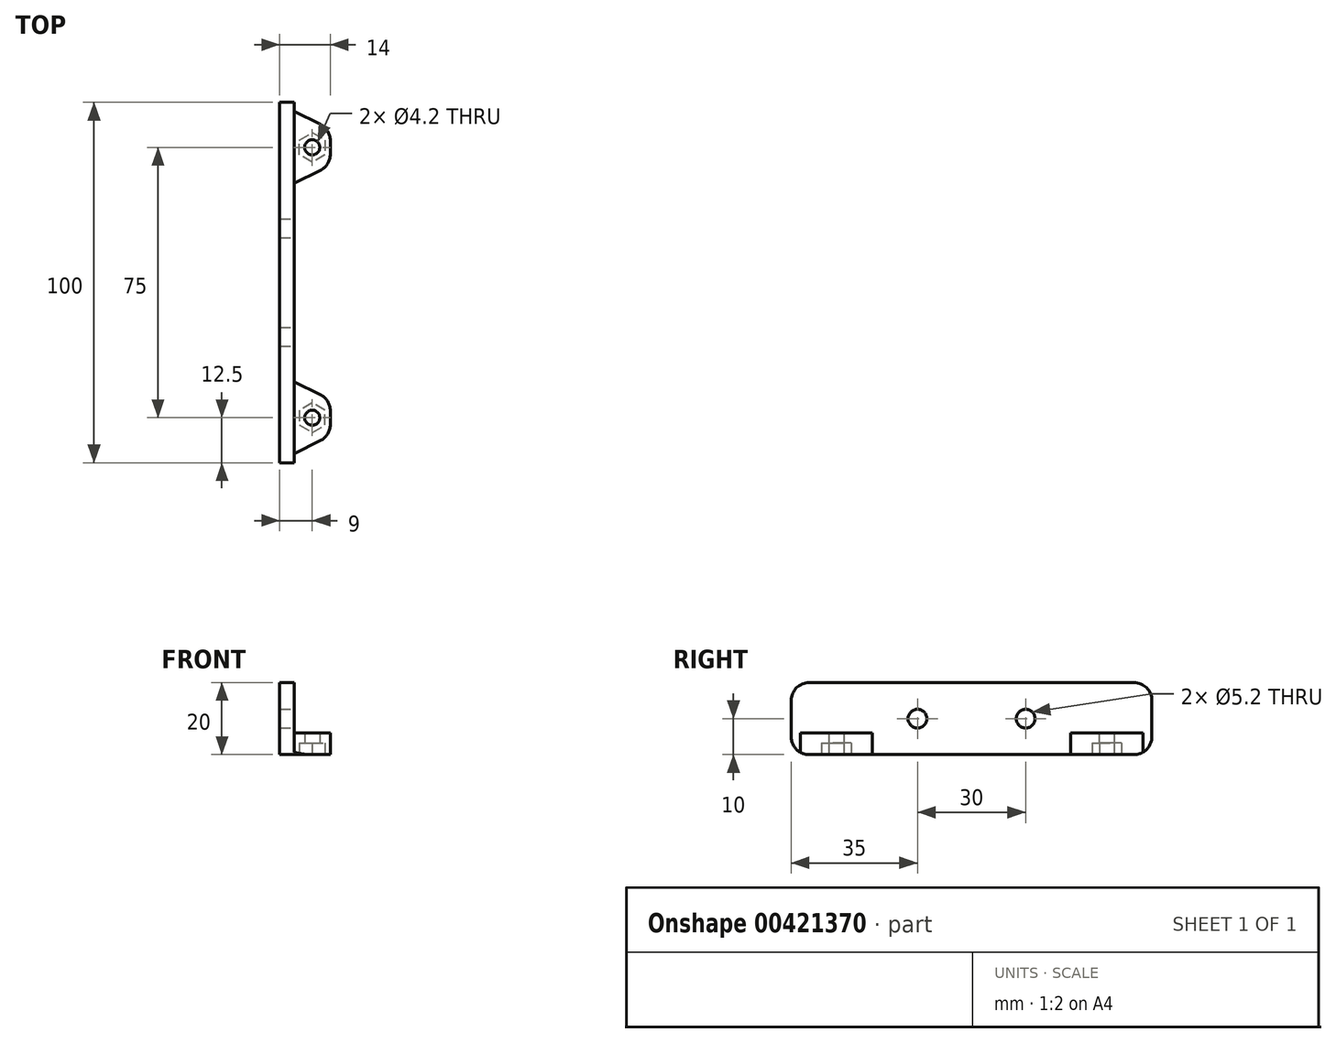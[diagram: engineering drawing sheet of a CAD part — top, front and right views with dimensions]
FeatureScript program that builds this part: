
annotation { "Feature Type Name" : "Feature", "Feature Type Description" : "" }
export const myFeature = defineFeature(function(context is Context, id is Id, definition is map)
    precondition{}
    {
        {
            var Q0;
            Q0=qCreatedBy(makeId("Right.planeOp"),FACE);
            var sketch = newSketch(context, id + "F0", { "sketchPlane" : qUnion([Q0])});
            skLineSegment(sketch, "E0.bottom", {"start": v(50, 10) * mm, "end": v(-50, 10) * mm});
            skLineSegment(sketch, "E0.top", {"start": v(50, -10) * mm, "end": v(-50, -10) * mm});
            skLineSegment(sketch, "E0.left", {"start": v(50, 10) * mm, "end": v(50, -10) * mm});
            skLineSegment(sketch, "E0.right", {"start": v(-50, 10) * mm, "end": v(-50, -10) * mm});
            skPoint(sketch, "E0.middle", {"position": v(0, 0) * mm});
            skLineSegment(sketch, "E1", {"start": v(0, 0) * mm, "end": v(-50, 0) * mm, "construction": true});
            skCircle(sketch, "E2", {"center": v(-15, 0) * mm, "radius": 2.6 * mm});
            skLineSegment(sketch, "E3", {"start": v(0, 10) * mm, "end": v(0, -10) * mm, "construction": true});
            skCircle(sketch, "E4.MirrorC", {"center": v(15, 0) * mm, "radius": 2.6 * mm});
            skSolve(sketch);
        }
        {
            var Q0;
            Q0 = qSketchRegion(id + "F0", true);
            extrude(context, id + "F1", {"entities" : qUnion([Q0]), "oppositeDirection" : true, "depth" : 4 * mm});
        }
        {
            var Q0;
            Q0=makeQuery(id+"F1.opExtrude","SWEPT_FACE",FACE,{"disambiguationData":[OSD([sQuery(id+"F0.wireOp",EDGE,"E0.top")])]});
            var sketch = newSketch(context, id + "F2", { "sketchPlane" : qUnion([Q0])});
            skLineSegment(sketch, "E5.0", {"start": v(0, -50) * mm, "end": v(0, 50) * mm, "construction": true});
            skLineSegment(sketch, "E6", {"start": v(0, 47.5) * mm, "end": v(7.24, 43.88) * mm});
            skLineSegment(sketch, "E7", {"start": v(10, 39.4) * mm, "end": v(10, 35.6) * mm});
            skLineSegment(sketch, "E8", {"start": v(7.24, 31.12) * mm, "end": v(0, 27.5) * mm});
            skCircle(sketch, "E9", {"center": v(5, 37.5) * mm, "radius": 2.1 * mm});
            skLineSegment(sketch, "E10", {"start": v(10, 37.5) * mm, "end": v(0, 37.5) * mm, "construction": true});
            skCircle(sketch, "E11.cCircle", {"center": v(5, 37.5) * mm, "radius": 3.55 * mm, "construction": true});
            skLineSegment(sketch, "E11.0", {"start": v(8.55, 39.55) * mm, "end": v(8.55, 35.45) * mm});
            skLineSegment(sketch, "E11.1", {"start": v(8.55, 35.45) * mm, "end": v(5, 33.4) * mm});
            skLineSegment(sketch, "E11.2", {"start": v(5, 33.4) * mm, "end": v(1.45, 35.45) * mm});
            skLineSegment(sketch, "E11.3", {"start": v(1.45, 35.45) * mm, "end": v(1.45, 39.55) * mm});
            skLineSegment(sketch, "E11.4", {"start": v(1.45, 39.55) * mm, "end": v(5, 41.6) * mm});
            skLineSegment(sketch, "E11.5", {"start": v(5, 41.6) * mm, "end": v(8.55, 39.55) * mm});
            skPoint(sketch, "E11.0.midPoint", {"position": v(8.55, 37.5) * mm});
            skPoint(sketch, "E12.visualSharp", {"position": v(10, 32.5) * mm});
            skArc(sketch, "E12.filletArc", {"start": v(7.24, 31.12) * mm, "mid": v(9.25, 32.96) * mm, "end": v(10, 35.6) * mm});
            skPoint(sketch, "E13.visualSharp", {"position": v(10, 42.5) * mm});
            skArc(sketch, "E13.filletArc", {"start": v(10, 39.4) * mm, "mid": v(9.25, 42.04) * mm, "end": v(7.24, 43.88) * mm});
            skSolve(sketch);
        }
        {
            var Q0;
            Q0 = qSketchRegion(id + "F2", true);
            var Q1;
            {var subQ0=sQuery(id+"F2.wireOp",EDGE,"E6");Q1=makeQuery(id+"F2.imprint","IMPRINT",FACE,{"disambiguationData":[TD([[makeQuery(id+"F2.imprint","IMPRINT",EDGE,{"derivedFrom":subQ0}),-1.0]])]});}
            extrude(context, id + "F3", {"entities" : qUnion([Q0, Q1]), "oppositeDirection" : true, "depth" : 6 * mm});
        }
        {
            var Q0;
            Q0=makeQuery(id+"F2.imprint","IMPRINT",FACE,{"disambiguationData":[TD([[makeQuery(id+"F2.imprint","IMPRINT",EDGE,{"derivedFrom":sQuery(id+"F2.wireOp",EDGE,"E9")}),-1.0]])]});
            extrude(context, id + "F4", {"entities" : qUnion([Q0]), "operationType" : NewBodyOperationType.REMOVE, "oppositeDirection" : true, "depth" : 3.2 * mm});
        }
        {
            var Q0;
            Q0=makeQuery(id+"F3.opExtrude","SWEPT_BODY",BODY,{"disambiguationData":[OSD([sQuery(id+"F0.wireOp",EDGE,"E0.top"),sQuery(id+"F2.wireOp",EDGE,"E6"),sQuery(id+"F2.wireOp",EDGE,"E7"),sQuery(id+"F2.wireOp",EDGE,"E8"),sQuery(id+"F2.wireOp",EDGE,"E9"),sQuery(id+"F2.wireOp",EDGE,"E12.filletArc"),sQuery(id+"F2.wireOp",EDGE,"E13.filletArc")])]});
            var Q1;
            Q1=qCreatedBy(makeId("Front.planeOp"),FACE);
            mirror(context, id + "F5", {"operationType" : NewBodyOperationType.ADD, "entities" : qUnion([Q0]), "mirrorPlane" : qUnion([Q1])});
        }
        {
            var Q0;
            Q0=makeQuery(id+"F1.opExtrude","SWEPT_EDGE",EDGE,{"disambiguationData":[OSD([sQuery(id+"F0.wireOp",EDGE,"E0.bottom"),sQuery(id+"F0.wireOp",EDGE,"E0.right")])]});
            var Q1;
            Q1=makeQuery(id+"F1.opExtrude","SWEPT_EDGE",EDGE,{"disambiguationData":[OSD([sQuery(id+"F0.wireOp",EDGE,"E0.top"),sQuery(id+"F0.wireOp",EDGE,"E0.right")])]});
            var Q2;
            Q2=makeQuery(id+"F1.opExtrude","SWEPT_EDGE",EDGE,{"disambiguationData":[OSD([sQuery(id+"F0.wireOp",EDGE,"E0.top"),sQuery(id+"F0.wireOp",EDGE,"E0.left")])]});
            var Q3;
            Q3=makeQuery(id+"F1.opExtrude","SWEPT_EDGE",EDGE,{"disambiguationData":[OSD([sQuery(id+"F0.wireOp",EDGE,"E0.bottom"),sQuery(id+"F0.wireOp",EDGE,"E0.left")])]});
            fillet(context, id + "F6", {"entities" : qUnion([Q0, Q1, Q2, Q3]), "radius" : 5 * mm, "tangentPropagation" : true, "allowEdgeOverflow" : false});
        }
    });
